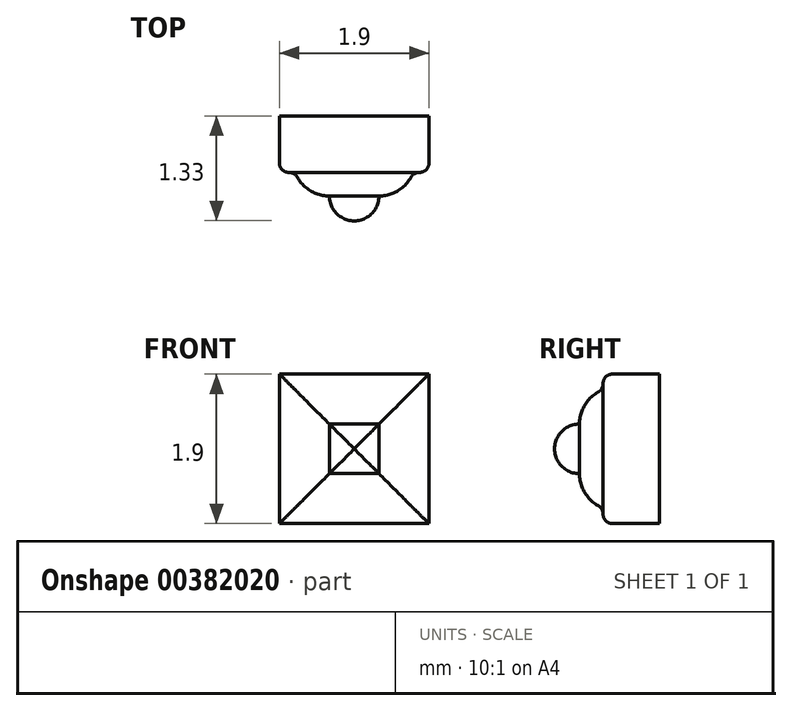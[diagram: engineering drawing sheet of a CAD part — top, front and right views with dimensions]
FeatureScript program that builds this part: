
annotation { "Feature Type Name" : "Feature", "Feature Type Description" : "" }
export const myFeature = defineFeature(function(context is Context, id is Id, definition is map)
    precondition{}
    {
        {
            var Q0;
            Q0=qCreatedBy(makeId("Front.planeOp"),FACE);
            var sketch = newSketch(context, id + "F0", { "sketchPlane" : qUnion([Q0])});
            skLineSegment(sketch, "E0.bottom", {"start": v(0, 0) * mm, "end": v(-0.95, 0) * mm});
            skLineSegment(sketch, "E0.top", {"start": v(0, 0.95) * mm, "end": v(-0.95, 0.95) * mm});
            skLineSegment(sketch, "E0.left", {"start": v(0, 0) * mm, "end": v(0, 0.95) * mm});
            skLineSegment(sketch, "E0.right", {"start": v(-0.95, 0) * mm, "end": v(-0.95, 0.95) * mm});
            skLineSegment(sketch, "E1.MirrorCS", {"start": v(0, -0.95) * mm, "end": v(-0.95, -0.95) * mm});
            skLineSegment(sketch, "E2.MirrorCS", {"start": v(-0.95, 0) * mm, "end": v(-0.95, -0.95) * mm});
            skLineSegment(sketch, "E3.MirrorCS", {"start": v(0, 0.95) * mm, "end": v(0.95, 0.95) * mm});
            skLineSegment(sketch, "E4.MirrorCS", {"start": v(0.95, 0) * mm, "end": v(0.95, 0.95) * mm});
            skLineSegment(sketch, "E5.MirrorCS", {"start": v(0, -0.95) * mm, "end": v(0.95, -0.95) * mm});
            skLineSegment(sketch, "E6.MirrorCS", {"start": v(0.95, 0) * mm, "end": v(0.95, -0.95) * mm});
            skSolve(sketch);
        }
        {
            var Q0;
            Q0 = qSketchRegion(id + "F0", true);
            extrude(context, id + "F1", {"entities" : qUnion([Q0]), "depth" : 0.72 * mm});
        }
        {
            var Q0;
            Q0=makeQuery(id+"F1.opExtrude","CAP_FACE",FACE,{"disambiguationData":[OSD([sQuery(id+"F0.wireOp",EDGE,"E0.top"),sQuery(id+"F0.wireOp",EDGE,"E0.right"),sQuery(id+"F0.wireOp",EDGE,"E1.MirrorCS"),sQuery(id+"F0.wireOp",EDGE,"E2.MirrorCS"),sQuery(id+"F0.wireOp",EDGE,"E3.MirrorCS"),sQuery(id+"F0.wireOp",EDGE,"E4.MirrorCS"),sQuery(id+"F0.wireOp",EDGE,"E5.MirrorCS"),sQuery(id+"F0.wireOp",EDGE,"E6.MirrorCS")])],"isStart":false});
            var sketch = newSketch(context, id + "F2", { "sketchPlane" : qUnion([Q0])});
            skLineSegment(sketch, "E7.bottom", {"start": v(0, 0) * mm, "end": v(-0.75, 0) * mm});
            skLineSegment(sketch, "E7.top", {"start": v(0, 0.75) * mm, "end": v(-0.75, 0.75) * mm});
            skLineSegment(sketch, "E7.left", {"start": v(0, 0) * mm, "end": v(0, 0.75) * mm});
            skLineSegment(sketch, "E7.right", {"start": v(-0.75, 0) * mm, "end": v(-0.75, 0.75) * mm});
            skLineSegment(sketch, "E8.MirrorCS", {"start": v(0.75, 0) * mm, "end": v(0.75, 0.75) * mm});
            skLineSegment(sketch, "E9.MirrorCS", {"start": v(0, 0.75) * mm, "end": v(0.75, 0.75) * mm});
            skLineSegment(sketch, "E10.MirrorCS", {"start": v(-0.75, 0) * mm, "end": v(-0.75, -0.75) * mm});
            skLineSegment(sketch, "E11.MirrorCS", {"start": v(0, -0.75) * mm, "end": v(-0.75, -0.75) * mm});
            skLineSegment(sketch, "E12.MirrorCS", {"start": v(0, -0.75) * mm, "end": v(0.75, -0.75) * mm});
            skLineSegment(sketch, "E13.MirrorCS", {"start": v(0.75, 0) * mm, "end": v(0.75, -0.75) * mm});
            skSolve(sketch);
        }
        {
            var Q0;
            Q0 = qSketchRegion(id + "F2", true);
            extrude(context, id + "F3", {"entities" : qUnion([Q0]), "operationType" : NewBodyOperationType.ADD, "depth" : 0.3 * mm});
        }
        {
            var Q0;
            Q0=makeQuery(id+"F3.opExtrude","CAP_FACE",FACE,{"disambiguationData":[OSD([sQuery(id+"F2.wireOp",EDGE,"E7.top"),sQuery(id+"F2.wireOp",EDGE,"E7.right"),sQuery(id+"F2.wireOp",EDGE,"E8.MirrorCS"),sQuery(id+"F2.wireOp",EDGE,"E9.MirrorCS"),sQuery(id+"F2.wireOp",EDGE,"E10.MirrorCS"),sQuery(id+"F2.wireOp",EDGE,"E11.MirrorCS"),sQuery(id+"F2.wireOp",EDGE,"E12.MirrorCS"),sQuery(id+"F2.wireOp",EDGE,"E13.MirrorCS")])],"isStart":false});
            fillet(context, id + "F4", {"entities" : qUnion([Q0]), "radius" : 0.47 * mm, "tangentPropagation" : true, "allowEdgeOverflow" : false});
        }
        {
            var Q0;
            Q0=makeQuery(id+"F3.opExtrude","CAP_FACE",FACE,{"disambiguationData":[OSD([sQuery(id+"F2.wireOp",EDGE,"E7.top"),sQuery(id+"F2.wireOp",EDGE,"E7.right"),sQuery(id+"F2.wireOp",EDGE,"E8.MirrorCS"),sQuery(id+"F2.wireOp",EDGE,"E9.MirrorCS"),sQuery(id+"F2.wireOp",EDGE,"E10.MirrorCS"),sQuery(id+"F2.wireOp",EDGE,"E11.MirrorCS"),sQuery(id+"F2.wireOp",EDGE,"E12.MirrorCS"),sQuery(id+"F2.wireOp",EDGE,"E13.MirrorCS")])],"isStart":false});
            var sketch = newSketch(context, id + "F5", { "sketchPlane" : qUnion([Q0])});
            skLineSegment(sketch, "E14.bottom", {"start": v(-0.32, 0.32) * mm, "end": v(0, 0.32) * mm});
            skLineSegment(sketch, "E14.top", {"start": v(-0.32, 0) * mm, "end": v(0, 0) * mm});
            skLineSegment(sketch, "E14.left", {"start": v(-0.32, 0.32) * mm, "end": v(-0.32, 0) * mm});
            skLineSegment(sketch, "E14.right", {"start": v(0, 0.32) * mm, "end": v(0, 0) * mm});
            skLineSegment(sketch, "E15.MirrorCS", {"start": v(0.32, 0.32) * mm, "end": v(0, 0.32) * mm});
            skLineSegment(sketch, "E16.MirrorCS", {"start": v(0.32, 0.32) * mm, "end": v(0.32, 0) * mm});
            skLineSegment(sketch, "E17.MirrorCS", {"start": v(0.32, -0.32) * mm, "end": v(0.32, 0) * mm});
            skLineSegment(sketch, "E18.MirrorCS", {"start": v(0.32, -0.32) * mm, "end": v(0, -0.32) * mm});
            skLineSegment(sketch, "E19.MirrorCS", {"start": v(-0.32, -0.32) * mm, "end": v(0, -0.32) * mm});
            skLineSegment(sketch, "E20.MirrorCS", {"start": v(-0.32, -0.32) * mm, "end": v(-0.32, 0) * mm});
            skSolve(sketch);
        }
        {
            var Q0;
            Q0 = qSketchRegion(id + "F5", true);
            extrude(context, id + "F6", {"entities" : qUnion([Q0]), "operationType" : NewBodyOperationType.ADD, "depth" : 0.32 * mm});
        }
        {
            var Q0;
            Q0=makeQuery(id+"F6.opExtrude","CAP_FACE",FACE,{"disambiguationData":[OSD([sQuery(id+"F5.wireOp",EDGE,"E14.bottom"),sQuery(id+"F5.wireOp",EDGE,"E14.left"),sQuery(id+"F5.wireOp",EDGE,"E15.MirrorCS"),sQuery(id+"F5.wireOp",EDGE,"E16.MirrorCS"),sQuery(id+"F5.wireOp",EDGE,"E17.MirrorCS"),sQuery(id+"F5.wireOp",EDGE,"E18.MirrorCS"),sQuery(id+"F5.wireOp",EDGE,"E19.MirrorCS"),sQuery(id+"F5.wireOp",EDGE,"E20.MirrorCS")])],"isStart":false});
            fillet(context, id + "F7", {"entities" : qUnion([Q0]), "radius" : 0.32 * mm, "tangentPropagation" : true, "allowEdgeOverflow" : false});
        }
        {
            var Q0;
            Q0=makeQuery(id+"F1.opExtrude","CAP_FACE",FACE,{"disambiguationData":[OSD([sQuery(id+"F0.wireOp",EDGE,"E0.top"),sQuery(id+"F0.wireOp",EDGE,"E0.right"),sQuery(id+"F0.wireOp",EDGE,"E1.MirrorCS"),sQuery(id+"F0.wireOp",EDGE,"E2.MirrorCS"),sQuery(id+"F0.wireOp",EDGE,"E3.MirrorCS"),sQuery(id+"F0.wireOp",EDGE,"E4.MirrorCS"),sQuery(id+"F0.wireOp",EDGE,"E5.MirrorCS"),sQuery(id+"F0.wireOp",EDGE,"E6.MirrorCS")])],"isStart":false});
            fillet(context, id + "F8", {"entities" : qUnion([Q0]), "radius" : 0.12 * mm, "tangentPropagation" : true, "allowEdgeOverflow" : false});
        }
    });
